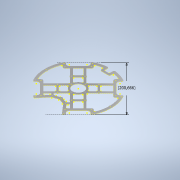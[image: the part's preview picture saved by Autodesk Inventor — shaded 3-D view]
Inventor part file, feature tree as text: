
AUTODESK INVENTOR PART (.ipt)
format: ipt  version: 2020 (Build 240168000, 168)  size: 1,358,848 bytes
history: native  units: mm
features: extrude x9, sketch x8, projected_geometry x6, other x1
ambient origin geometry x8: Origin, YZ Plane, XZ Plane, XY Plane, X Axis, Y Axis, Z Axis, Center Point
bodies: Body1 (feature_tree)
feature tree (24):
  other  "Твердое тело1"
  extrude  "outer"  TaperAngle=45.0deg  [1 undecoded]
  extrude  "inner"  Depth=7.0mm
  sketch  "Эскиз3"
  extrude  "Выдавливание3"  Depth=20.0mm
  extrude  "Выдавливание4"  Depth=7.0mm
  extrude  "Выдавливание5"  Depth=3.2mm
  sketch  "Эскиз5"
  extrude  "Выдавливание7"  Depth=59.0mm
  extrude  "Выдавливание8"  Depth=83.0mm
  sketch  "Эскиз6"
  extrude  "Выдавливание9"  Depth=69.0mm
  extrude  "Выдавливание10"  Depth=55.0mm
  sketch  "Эскиз7"
  sketch  "Эскиз8"
  sketch  "Эскиз1"
  sketch  "Эскиз2"
  projected_geometry  "Спроецированная петля1"
  projected_geometry  "Спроецированная петля2"
  sketch  "Эскиз4"
  projected_geometry  "Спроецированная петля3"
  projected_geometry  "Спроецированная петля4"
  projected_geometry  "Спроецированная петля5"
  projected_geometry  "Спроецированная петля6"
note: 1 required parameter value undecoded (feature->parameter linkage not recoverable at this tier; creation-order binding heuristic only, values carry confidence <= 0.55)
